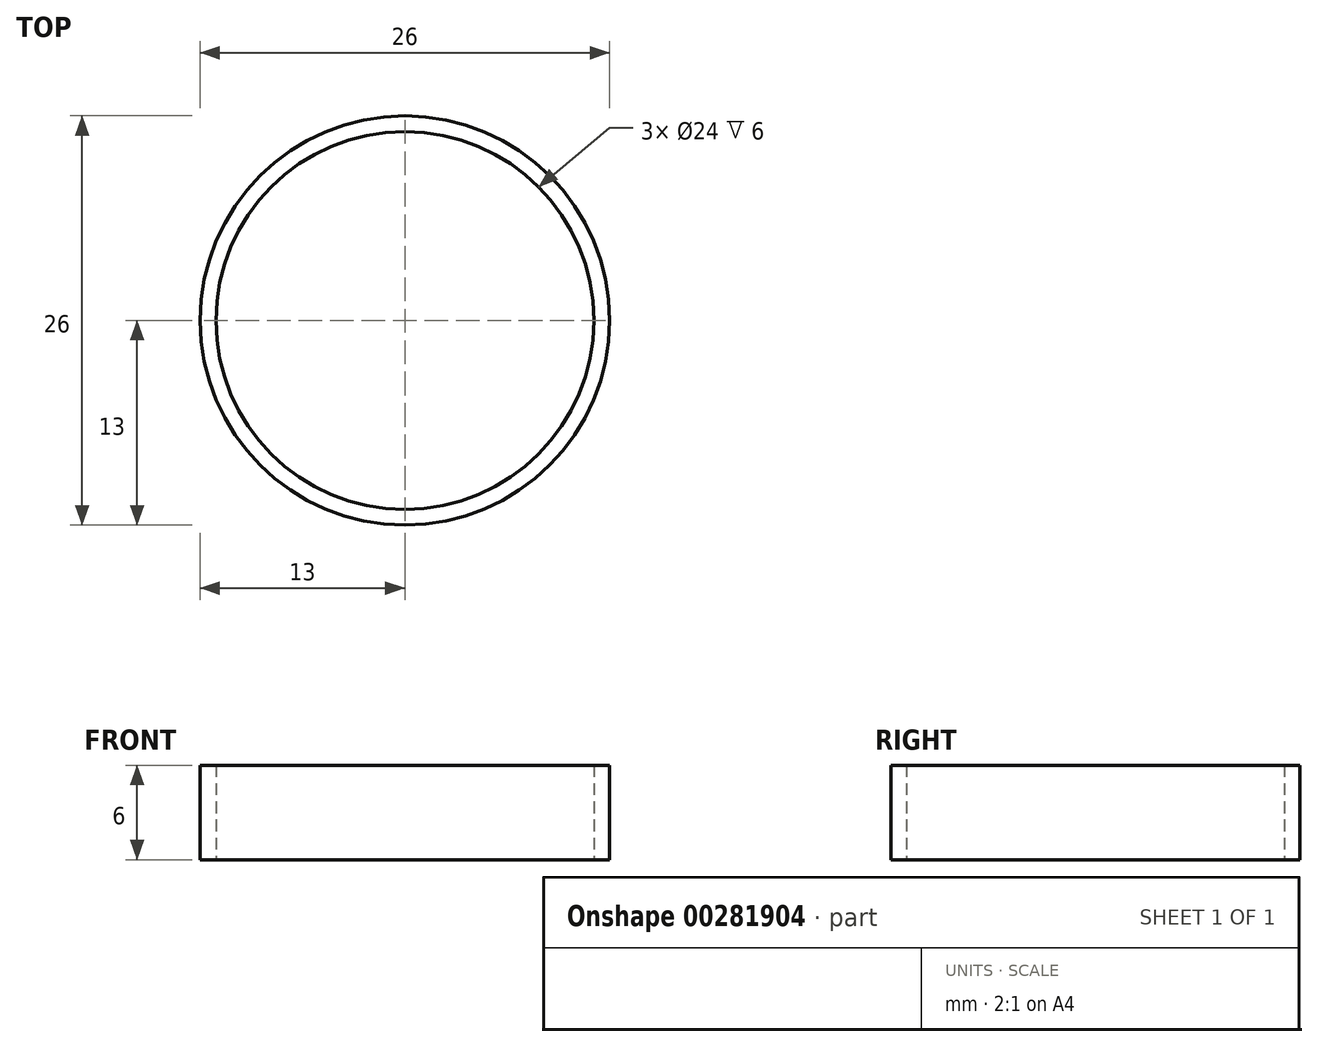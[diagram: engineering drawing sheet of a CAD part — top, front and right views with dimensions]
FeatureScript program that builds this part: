
annotation { "Feature Type Name" : "Feature", "Feature Type Description" : "" }
export const myFeature = defineFeature(function(context is Context, id is Id, definition is map)
    precondition{}
    {
        {
            var Q0;
            Q0=qCreatedBy(makeId("Top.planeOp"),FACE);
            var sketch = newSketch(context, id + "F0", { "sketchPlane" : qUnion([Q0])});
            skCircle(sketch, "E0", {"center": v(0, 0) * mm, "radius": 12 * mm});
            skCircle(sketch, "E1", {"center": v(0, 0) * mm, "radius": 13 * mm});
            skSolve(sketch);
        }
        {
            var Q0;
            Q0=qSketchRegion(id+"F0",true);
            extrude(context, id + "F1", {"entities" : qUnion([Q0]), "depth" : 6 * mm});
        }
    });
